# Revit family: 636-00-001-DN80-300
name_source: partatom
category: Pipe Accessories
units: mm (PartAtom-declared; Revit-internal decimal feet)

## family parameters
Always vertical = No
Cut with Voids When Loaded = No
Part Type = Valve - Breaks Into
Round Connector Dimension = Use Diameter
Shared = No
Work Plane-Based = No

## types (8) — shared parameters
Body_Wallthickness = 15 mm  [stored 0.0492126 ft]
DN080_PN16 = 636-080-00-040064
DN100_PN16 = 636-100-00-040064
DN125_PN16 = 636-125-00-040064
DN150_PN16 = 636-150-00-040064
DN200_ PN16 = 636-200-00-040064
DN200_PN16 = 636-205-00-040064
DN250_PN16 = 636-250-00-040064
DN300_PN16 = 636-300-00-040064
Description_ = AVK GATE VALVE, SUPA MAXI™
Ftc = 4 mm  [stored 0.0131234 ft]
Name_Height_reference = 10 mm  [stored 0.0328084 ft]
Rib_Thickness = 18 mm  [stored 0.0590551 ft]
Search_table = 636-00-001-DN80-300
URL product pages = https://www.avkvalves.com
zero-valued in all types: Bottom_Reference

## per-type parameters (varying)
- DN100_PN16: At=83 mm; Body_Height=122 mm; Body_depth=166 mm; Body_width=80 mm; Bonnet_Flange_Depth=192 mm; Bonnet_Flange_Width=81 mm; Bonnet_Flange_cut=8 mm  [stored 0.0262467 ft]; Bonnet_Flange_thickness=15 mm  [stored 0.0492126 ft]; Bonnet_Height=55 mm  [stored 0.180446 ft]; Bonnet_Reference_height=112 mm; Bonnet_Thickness=82 mm; Bt=82 mm; Bt_2=74 mm; CL _Thickness=29 mm  [stored 0.0951444 ft]; CL_Height=88 mm; Cut_Reference=916 mm; D=237 mm; D1=10 mm  [stored 0.0328084 ft]; D2=38 mm  [stored 0.124672 ft]; D_ref=198 mm; D_ref_2=82 mm; E=15 mm  [stored 0.0492126 ft]; F=10 mm  [stored 0.0328084 ft]; F1=22 mm  [stored 0.0721785 ft]; Fillet_Thickness=6 mm  [stored 0.019685 ft]; Flange_OR=110 mm; Flange_Thickness=19 mm  [stored 0.062336 ft]; Flange_Thickness_cut=30 mm  [stored 0.0984252 ft]; Ftc_reference_height=110 mm; H=305 mm; H1=267 mm; H3=426 mm; Horizontal_Flange_width=242 mm; ID (Radius)=50 mm  [stored 0.164042 ft]; L=458 mm; L_Dia=100 mm; L_ref=305 mm; L_ref_2=183 mm; Name_Reference=101 mm; Name_Width=40 mm  [stored 0.131234 ft]; Neck_H=57 mm  [stored 0.187008 ft]; Neck_T=27 mm  [stored 0.0885827 ft]; Neck_T2=25 mm  [stored 0.082021 ft]; Nominal Diameter (DN)=100 mm; R1tv=1100 mm; R2f=15 mm  [stored 0.0492126 ft]; RF_Dia=78 mm; Rf=403 mm; Rib_Height_Reference_1=120 mm; Rib_Height_Reference_2=110 mm; Rib_Height_Reference_3=100 mm; Rib_Height_Reference_4=90 mm; Rib_Width_1=40 mm  [stored 0.131234 ft]; Rib_Width_2=40 mm  [stored 0.131234 ft]; Rib_Width_3=40 mm  [stored 0.131234 ft]; Rib_depth_1=40 mm  [stored 0.131234 ft]; Rib_depth_2=40 mm  [stored 0.131234 ft]; Rib_depth_3=40 mm  [stored 0.131234 ft]; Rt=367 mm; T=119 mm
- DN125_PN16: At=97 mm; Body_Height=137 mm; Body_depth=194 mm; Body_width=90 mm; Bonnet_Flange_Depth=220 mm; Bonnet_Flange_Width=83 mm; Bonnet_Flange_cut=8 mm  [stored 0.0262467 ft]; Bonnet_Flange_thickness=15 mm  [stored 0.0492126 ft]; Bonnet_Height=63 mm  [stored 0.206693 ft]; Bonnet_Reference_height=127 mm; Bonnet_Thickness=92 mm; Bt=92 mm; Bt_2=84 mm; CL _Thickness=34 mm  [stored 0.111549 ft]; CL_Height=102 mm; Cut_Reference=902 mm; D=253 mm; D1=10 mm  [stored 0.0328084 ft]; D2=38 mm  [stored 0.124672 ft]; D_ref=211 mm; D_ref_2=88 mm; E=15 mm  [stored 0.0492126 ft]; F=10 mm  [stored 0.0328084 ft]; F1=22 mm  [stored 0.0721785 ft]; Fillet_Thickness=6 mm  [stored 0.019685 ft]; Flange_OR=125 mm; Flange_Thickness=19 mm  [stored 0.062336 ft]; Flange_Thickness_cut=31 mm; Ftc_reference_height=125 mm; H=346 mm; H1=308 mm; H3=475 mm; Horizontal_Flange_width=258 mm; ID (Radius)=63 mm  [stored 0.206693 ft]; L=451 mm; L_Dia=125 mm; L_ref=301 mm; L_ref_2=180 mm; Name_Reference=114 mm; Name_Width=45 mm  [stored 0.147638 ft]; Neck_H=69 mm; Neck_T=32 mm  [stored 0.104987 ft]; Neck_T2=30 mm  [stored 0.0984252 ft]; Nominal Diameter (DN)=125 mm; R1tv=1250 mm; R2f=15 mm  [stored 0.0492126 ft]; RF_Dia=92 mm; Rf=430 mm; Rib_Height_Reference_1=120 mm; Rib_Height_Reference_2=110 mm; Rib_Height_Reference_3=100 mm; Rib_Height_Reference_4=120 mm; Rib_Width_1=45 mm  [stored 0.147638 ft]; Rib_Width_2=45 mm  [stored 0.147638 ft]; Rib_Width_3=45 mm  [stored 0.147638 ft]; Rib_depth_1=45 mm  [stored 0.147638 ft]; Rib_depth_2=45 mm  [stored 0.147638 ft]; Rib_depth_3=45 mm  [stored 0.147638 ft]; Rt=417 mm; T=146 mm
- DN150_PN16: At=121 mm; Body_Height=172 mm; Body_depth=242 mm; Body_width=95 mm; Bonnet_Flange_Depth=272 mm; Bonnet_Flange_Width=116 mm; Bonnet_Flange_cut=8 mm  [stored 0.0262467 ft]; Bonnet_Flange_thickness=15 mm  [stored 0.0492126 ft]; Bonnet_Height=71 mm; Bonnet_Reference_height=162 mm; Bonnet_Thickness=97 mm; Bt=97 mm; Bt_2=89 mm; CL _Thickness=34 mm  [stored 0.111549 ft]; CL_Height=126 mm; Cut_Reference=998 mm; D=309 mm; D1=10 mm  [stored 0.0328084 ft]; D2=38 mm  [stored 0.124672 ft]; D_ref=258 mm; D_ref_2=107 mm; E=15 mm  [stored 0.0492126 ft]; F=10 mm  [stored 0.0328084 ft]; F1=22 mm  [stored 0.0721785 ft]; Fillet_Thickness=12 mm  [stored 0.0393701 ft]; Flange_OR=142 mm; Flange_Thickness=19 mm  [stored 0.062336 ft]; Flange_Thickness_cut=34 mm  [stored 0.111549 ft]; Ftc_reference_height=142 mm; H=400 mm; H1=362 mm; H3=557 mm; Horizontal_Flange_width=314 mm; ID (Radius)=75 mm; L=499 mm; L_Dia=150 mm; L_ref=333 mm; L_ref_2=200 mm; Name_Reference=143 mm; Name_Width=48 mm  [stored 0.15748 ft]; Neck_H=64 mm; Neck_T=32 mm  [stored 0.104987 ft]; Neck_T2=30 mm  [stored 0.0984252 ft]; Nominal Diameter (DN)=150 mm; R1tv=1420 mm; R2f=30 mm  [stored 0.0984252 ft]; RF_Dia=106 mm; Rf=523 mm; Rib_Height_Reference_1=120 mm; Rib_Height_Reference_2=110 mm; Rib_Height_Reference_3=100 mm; Rib_Height_Reference_4=150 mm; Rib_Width_1=48 mm  [stored 0.15748 ft]; Rib_Width_2=48 mm  [stored 0.15748 ft]; Rib_Width_3=48 mm  [stored 0.15748 ft]; Rib_depth_1=48 mm  [stored 0.15748 ft]; Rib_depth_2=48 mm  [stored 0.15748 ft]; Rib_depth_3=48 mm  [stored 0.15748 ft]; Rt=473 mm; T=174 mm
- DN200_PN 16: At=147 mm; Body_Height=220 mm; Body_depth=294 mm; Body_width=108 mm; Bonnet_Flange_Depth=332 mm; Bonnet_Flange_Width=132 mm; Bonnet_Flange_cut=13 mm; Bonnet_Flange_thickness=25 mm  [stored 0.082021 ft]; Bonnet_Height=85 mm; Bonnet_Reference_height=210 mm; Bonnet_Thickness=110 mm; Bt=110 mm; Bt_2=102 mm; CL _Thickness=34 mm  [stored 0.111549 ft]; CL_Height=152 mm; Cut_Reference=1098 mm; D=359 mm; D1=10 mm  [stored 0.0328084 ft]; D2=42 mm  [stored 0.137795 ft]; D_ref=299 mm; D_ref_2=125 mm; E=15 mm  [stored 0.0492126 ft]; F=12 mm  [stored 0.0393701 ft]; F1=28 mm  [stored 0.0918635 ft]; Fillet_Thickness=24 mm  [stored 0.0787402 ft]; Flange_OR=170 mm; Flange_Thickness=20 mm  [stored 0.0656168 ft]; Flange_Thickness_cut=35 mm  [stored 0.114829 ft]; Ftc_reference_height=170 mm; H=490 mm; H1=448 mm; H3=672 mm; Horizontal_Flange_width=364 mm; ID (Radius)=100 mm; L=549 mm; L_Dia=200 mm; L_ref=366 mm; L_ref_2=220 mm; Name_Reference=183 mm; Name_Width=54 mm  [stored 0.177165 ft]; Neck_H=76 mm; Neck_T=32 mm  [stored 0.104987 ft]; Neck_T2=30 mm  [stored 0.0984252 ft]; Nominal Diameter (DN)=200 mm; R1tv=1700 mm; R2f=60 mm  [stored 0.19685 ft]; RF_Dia=133 mm; Rf=607 mm; Rib_Height_Reference_1=120 mm; Rib_Height_Reference_2=110 mm; Rib_Height_Reference_3=100 mm; Rib_Height_Reference_4=180 mm; Rib_Width_1=54 mm  [stored 0.177165 ft]; Rib_Width_2=54 mm  [stored 0.177165 ft]; Rib_Width_3=54 mm  [stored 0.177165 ft]; Rib_depth_1=54 mm  [stored 0.177165 ft]; Rib_depth_2=54 mm  [stored 0.177165 ft]; Rib_depth_3=54 mm  [stored 0.177165 ft]; Rt=567 mm; T=210 mm
- DN200_PN16: At=147 mm; Body_Height=220 mm; Body_depth=294 mm; Body_width=108 mm; Bonnet_Flange_Depth=332 mm; Bonnet_Flange_Width=132 mm; Bonnet_Flange_cut=13 mm; Bonnet_Flange_thickness=25 mm  [stored 0.082021 ft]; Bonnet_Height=85 mm; Bonnet_Reference_height=210 mm; Bonnet_Thickness=110 mm; Bt=110 mm; Bt_2=102 mm; CL _Thickness=34 mm  [stored 0.111549 ft]; CL_Height=152 mm; Cut_Reference=1080 mm; D=396 mm; D1=10 mm  [stored 0.0328084 ft]; D2=42 mm  [stored 0.137795 ft]; D_ref=330 mm; D_ref_2=138 mm; E=15 mm  [stored 0.0492126 ft]; F=12 mm  [stored 0.0393701 ft]; F1=28 mm  [stored 0.0918635 ft]; Fillet_Thickness=24 mm  [stored 0.0787402 ft]; Flange_OR=170 mm; Flange_Thickness=20 mm  [stored 0.0656168 ft]; Flange_Thickness_cut=35 mm  [stored 0.114829 ft]; Ftc_reference_height=170 mm; H=490 mm; H1=448 mm; H3=690 mm; Horizontal_Flange_width=400 mm; ID (Radius)=100 mm; L=540 mm; L_Dia=200 mm; L_ref=360 mm; L_ref_2=216 mm; Name_Reference=183 mm; Name_Width=54 mm  [stored 0.177165 ft]; Neck_H=76 mm; Neck_T=32 mm  [stored 0.104987 ft]; Neck_T2=30 mm  [stored 0.0984252 ft]; Nominal Diameter (DN)=200 mm; R1tv=1700 mm; R2f=60 mm  [stored 0.19685 ft]; RF_Dia=133 mm; Rf=667 mm; Rib_Height_Reference_1=120 mm; Rib_Height_Reference_2=110 mm; Rib_Height_Reference_3=100 mm; Rib_Height_Reference_4=180 mm; Rib_Width_1=54 mm  [stored 0.177165 ft]; Rib_Width_2=54 mm  [stored 0.177165 ft]; Rib_Width_3=54 mm  [stored 0.177165 ft]; Rib_depth_1=54 mm  [stored 0.177165 ft]; Rib_depth_2=54 mm  [stored 0.177165 ft]; Rib_depth_3=54 mm  [stored 0.177165 ft]; Rt=567 mm; T=241 mm
- DN250_PN16: At=171 mm; Body_Height=305 mm; Body_depth=342 mm; Body_width=124 mm; Bonnet_Flange_Depth=372 mm; Bonnet_Flange_Width=158 mm; Bonnet_Flange_cut=13 mm; Bonnet_Flange_thickness=25 mm  [stored 0.082021 ft]; Bonnet_Height=100 mm; Bonnet_Reference_height=295 mm; Bonnet_Thickness=126 mm; Bt=126 mm; Bt_2=118 mm; CL _Thickness=42 mm  [stored 0.137795 ft]; CL_Height=176 mm; Cut_Reference=1172 mm; D=431 mm; D1=15 mm  [stored 0.0492126 ft]; D2=55 mm  [stored 0.180446 ft]; D_ref=359 mm; D_ref_2=150 mm; E=13 mm; F=14 mm  [stored 0.0459318 ft]; F1=37 mm  [stored 0.121391 ft]; Fillet_Thickness=24 mm  [stored 0.0787402 ft]; Flange_OR=200 mm; Flange_Thickness=22 mm  [stored 0.0721785 ft]; Flange_Thickness_cut=38 mm  [stored 0.124672 ft]; Ftc_reference_height=200 mm; H=664 mm; H1=609 mm; H3=885 mm; Horizontal_Flange_width=442 mm; ID (Radius)=125 mm; L=586 mm; L_Dia=250 mm; L_ref=391 mm; L_ref_2=234 mm; Name_Reference=270 mm; Name_Width=62 mm  [stored 0.203412 ft]; Neck_H=128 mm; Neck_T=40 mm  [stored 0.131234 ft]; Neck_T2=38 mm  [stored 0.124672 ft]; Nominal Diameter (DN)=250 mm; R1tv=2000 mm; R2f=60 mm  [stored 0.19685 ft]; RF_Dia=160 mm; Rf=737 mm; Rib_Height_Reference_1=90 mm; Rib_Height_Reference_2=110 mm; Rib_Height_Reference_3=100 mm; Rib_Height_Reference_4=200 mm; Rib_Width_1=140 mm; Rib_Width_2=140 mm; Rib_Width_3=62 mm  [stored 0.203412 ft]; Rib_depth_1=372 mm; Rib_depth_2=62 mm  [stored 0.203412 ft]; Rib_depth_3=62 mm  [stored 0.203412 ft]; Rt=667 mm; T=284 mm
- DN300_PN16: At=209 mm; Body_Height=370 mm; Body_depth=418 mm; Body_width=157 mm; Bonnet_Flange_Depth=432 mm; Bonnet_Flange_Width=206 mm; Bonnet_Flange_cut=18 mm  [stored 0.0590551 ft]; Bonnet_Flange_thickness=35 mm  [stored 0.114829 ft]; Bonnet_Height=114 mm; Bonnet_Reference_height=360 mm; Bonnet_Thickness=160 mm; Bt=160 mm; Bt_2=151 mm; CL _Thickness=59 mm; CL_Height=214 mm; Cut_Reference=1318 mm; D=510 mm; D1=15 mm  [stored 0.0492126 ft]; D2=55 mm  [stored 0.180446 ft]; D_ref=425 mm; D_ref_2=177 mm; E=13 mm; F=14 mm  [stored 0.0459318 ft]; F1=37 mm  [stored 0.121391 ft]; Fillet_Thickness=24 mm  [stored 0.0787402 ft]; Flange_OR=228 mm; Flange_Thickness=25 mm  [stored 0.082021 ft]; Flange_Thickness_cut=39 mm  [stored 0.127953 ft]; Ftc_reference_height=228 mm; H=740 mm; H1=685 mm; H3=993 mm; Horizontal_Flange_width=506 mm; ID (Radius)=150 mm; L=659 mm; L_Dia=300 mm; L_ref=439 mm; L_ref_2=264 mm; Name_Reference=250 mm; Name_Width=79 mm; Neck_H=101 mm; Neck_T=57 mm  [stored 0.187008 ft]; Neck_T2=55 mm  [stored 0.180446 ft]; Nominal Diameter (DN)=300 mm; R1tv=2280 mm; R2f=60 mm  [stored 0.19685 ft]; RF_Dia=185 mm; Rf=843 mm; Rib_Height_Reference_1=178 mm; Rib_Height_Reference_2=285 mm; Rib_Height_Reference_3=150 mm; Rib_Height_Reference_4=300 mm; Rib_Width_1=180 mm; Rib_Width_2=180 mm; Rib_Width_3=79 mm; Rib_depth_1=432 mm; Rib_depth_2=432 mm; Rib_depth_3=79 mm; Rt=760 mm; T=335 mm
- DN080_PN16: At=70 mm; Body_Height=108 mm; Body_depth=140 mm; Body_width=75 mm; Bonnet_Flange_Depth=171 mm; Bonnet_Flange_Width=76 mm; Bonnet_Flange_cut=8 mm  [stored 0.0262467 ft]; Bonnet_Flange_thickness=15 mm  [stored 0.0492126 ft]; Bonnet_Height=50 mm  [stored 0.164042 ft]; Bonnet_Reference_height=98 mm; Bonnet_Thickness=77 mm; Bt=77 mm; Bt_2=69 mm; CL _Thickness=27 mm  [stored 0.0885827 ft]; CL_Height=75 mm; Cut_Reference=910 mm; D=214 mm; D1=10 mm  [stored 0.0328084 ft]; D2=34 mm  [stored 0.111549 ft]; D_ref=178 mm; D_ref_2=74 mm; E=15 mm  [stored 0.0492126 ft]; F=9 mm; F1=20 mm  [stored 0.0656168 ft]; Fillet_Thickness=6 mm  [stored 0.019685 ft]; Flange_OR=100 mm; Flange_Thickness=19 mm  [stored 0.062336 ft]; Flange_Thickness_cut=30 mm  [stored 0.0984252 ft]; Ftc_reference_height=100 mm; H=281 mm; H1=247 mm; H3=380 mm; Horizontal_Flange_width=198 mm; ID (Radius)=40 mm  [stored 0.131234 ft]; L=455 mm; L_Dia=80 mm; L_ref=303 mm; L_ref_2=182 mm; Name_Reference=90 mm; Name_Width=38 mm  [stored 0.124672 ft]; Neck_H=64 mm; Neck_T=25 mm  [stored 0.082021 ft]; Neck_T2=23 mm; Nominal Diameter (DN)=80 mm; R1tv=1000 mm; R2f=15 mm  [stored 0.0492126 ft]; RF_Dia=66 mm; Rf=330 mm; Rib_Height_Reference_1=120 mm; Rib_Height_Reference_2=110 mm; Rib_Height_Reference_3=100 mm; Rib_Height_Reference_4=85 mm; Rib_Width_1=38 mm  [stored 0.124672 ft]; Rib_Width_2=38 mm  [stored 0.124672 ft]; Rib_Width_3=38 mm  [stored 0.124672 ft]; Rib_depth_1=38 mm  [stored 0.124672 ft]; Rib_depth_2=38 mm  [stored 0.124672 ft]; Rib_depth_3=38 mm  [stored 0.124672 ft]; Rt=333 mm; T=94 mm

note: [stored X ft] marks values corroborated as IEEE doubles in the binary element streams (Revit-internal decimal feet)

## geometry (parser evidence)
native form markers: Extrusion x1, Sweep x3
no freeform markers — native parametric forms only
